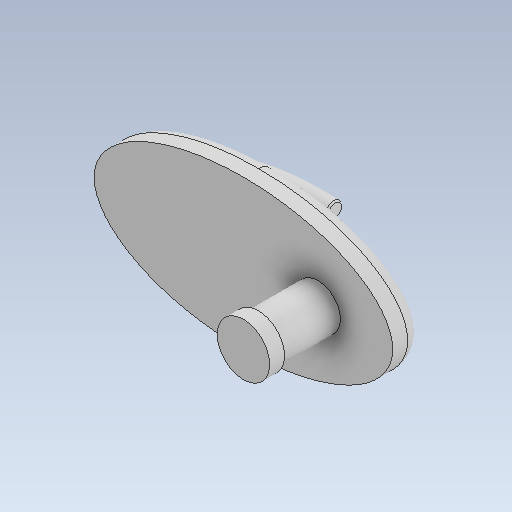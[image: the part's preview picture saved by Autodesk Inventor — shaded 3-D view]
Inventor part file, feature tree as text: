
AUTODESK INVENTOR PART (.ipt)
format: ipt  version: 2020.3 (Build 243373000, 373)  size: 234,496 bytes
history: native  units: mm
features: sketch x4, extrude x2, fillet x2, sweep x1, thicken_offset x1, direct_edit x1, other x1
ambient origin geometry x8: Origin, YZ Plane, XZ Plane, XY Plane, X Axis, Y Axis, Z Axis, Center Point
bodies: Solid1 (feature_tree), Solid2 (feature_tree)
feature tree (12):
  extrude  "Extrusion1"  Depth=3.0mm
  extrude  "Extrusion2"  Depth=2.0mm
  sweep  "Sweep1"
  fillet  "Fillet1"  Radius=0.1mm
  fillet  "Fillet2"  Radius=1.0mm
  thicken_offset  "Thicken1"
  direct_edit  "Direct Edit1"
  sketch  "Sketch1"  dims[d2=2.0mm d3=0.0mm d4=3.0mm]
  sketch  "Sketch2"  dims[d5=4.0mm d6=0.0mm d7=2.0mm]
  sketch  "Sketch3"  dims[d8=-0.523599mm d9=0.0mm d10=1.0mm d11=0.1mm d12=1.0mm]
  sketch  "Sketch4"  dims[d13=1.0mm d14=0.25mm]
  other  "Size1"
